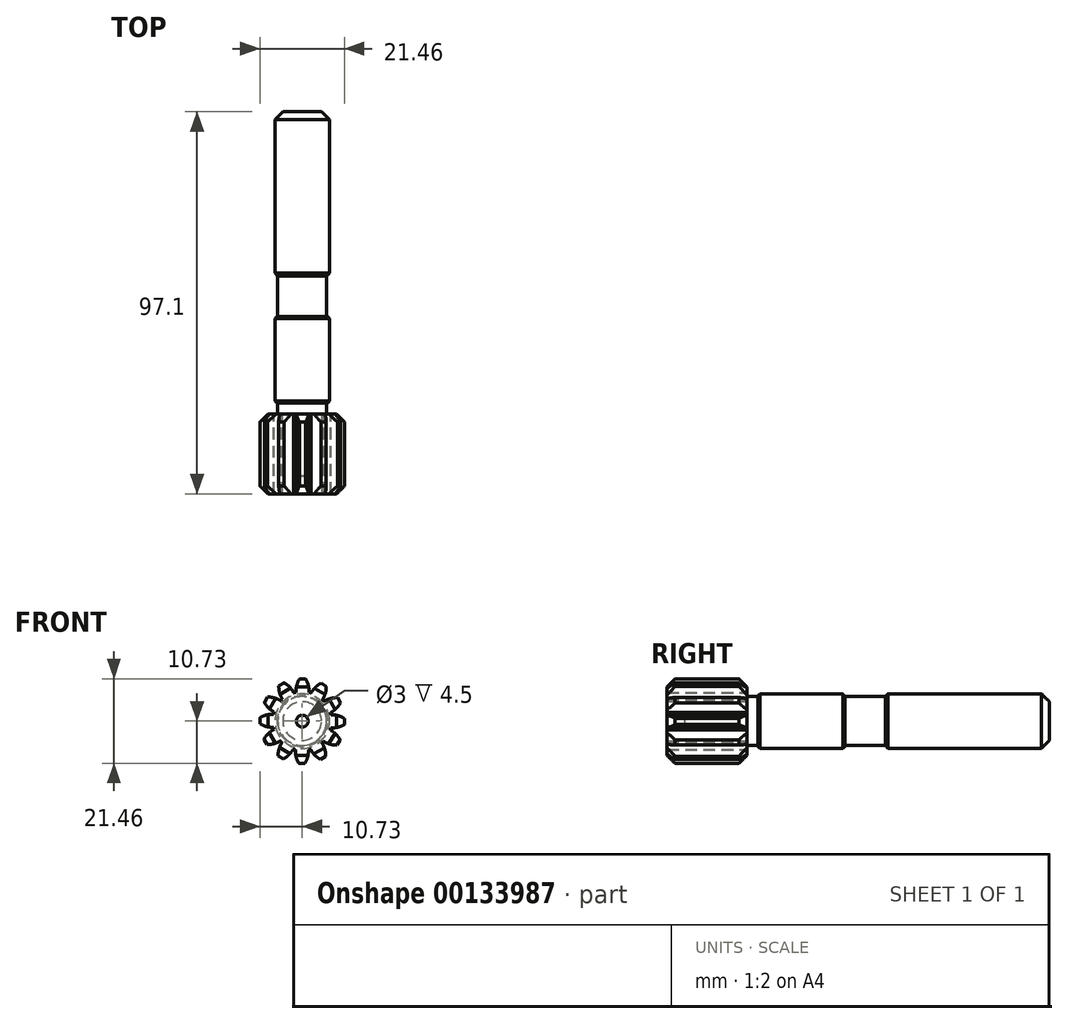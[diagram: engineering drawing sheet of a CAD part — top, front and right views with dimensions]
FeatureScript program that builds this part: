
annotation { "Feature Type Name" : "Feature", "Feature Type Description" : "" }
export const myFeature = defineFeature(function(context is Context, id is Id, definition is map)
    precondition{}
    {
        {
            var Q0;
            Q0=qCreatedBy(makeId("Front.planeOp"),FACE);
            var sketch = newSketch(context, id + "F0", { "sketchPlane" : qUnion([Q0])});
            skCircle(sketch, "E0", {"center": v(0, 0) * mm, "radius": 7.5 * mm});
            skCircle(sketch, "E1", {"center": v(0, 0) * mm, "radius": 10.75 * mm, "construction": true});
            skCircle(sketch, "E2", {"center": v(0, 0) * mm, "radius": 8.75 * mm, "construction": true});
            skArc(sketch, "E3", {"start": v(-0.67, 10.73) * mm, "mid": v(-1.38, 9.1) * mm, "end": v(-1.58, 7.33) * mm});
            skArc(sketch, "E4", {"start": v(1.73, 7.3) * mm, "mid": v(1.56, 9.07) * mm, "end": v(0.88, 10.71) * mm});
            skLineSegment(sketch, "E5", {"start": v(-0.67, 10.73) * mm, "end": v(0.88, 10.71) * mm});
            skLineSegment(sketch, "E6.1.0", {"start": v(-5.95, 8.95) * mm, "end": v(-4.6, 9.72) * mm});
            skArc(sketch, "E6.1.1", {"start": v(-2.15, 7.19) * mm, "mid": v(-3.18, 8.63) * mm, "end": v(-4.6, 9.72) * mm});
            skArc(sketch, "E6.1.2", {"start": v(-5.95, 8.95) * mm, "mid": v(-5.75, 7.19) * mm, "end": v(-5.04, 5.56) * mm});
            skLineSegment(sketch, "E6.2.0", {"start": v(-9.63, 4.78) * mm, "end": v(-8.84, 6.12) * mm});
            skArc(sketch, "E6.2.1", {"start": v(-5.45, 5.15) * mm, "mid": v(-7.07, 5.89) * mm, "end": v(-8.84, 6.12) * mm});
            skArc(sketch, "E6.2.2", {"start": v(-9.63, 4.78) * mm, "mid": v(-8.57, 3.35) * mm, "end": v(-7.14, 2.3) * mm});
            skLineSegment(sketch, "E6.3.0", {"start": v(-10.73, -0.67) * mm, "end": v(-10.71, 0.88) * mm});
            skArc(sketch, "E6.3.1", {"start": v(-7.3, 1.73) * mm, "mid": v(-9.07, 1.56) * mm, "end": v(-10.71, 0.88) * mm});
            skArc(sketch, "E6.3.2", {"start": v(-10.73, -0.67) * mm, "mid": v(-9.1, -1.38) * mm, "end": v(-7.33, -1.58) * mm});
            skLineSegment(sketch, "E6.4.0", {"start": v(-8.95, -5.95) * mm, "end": v(-9.72, -4.6) * mm});
            skArc(sketch, "E6.4.1", {"start": v(-7.19, -2.15) * mm, "mid": v(-8.63, -3.18) * mm, "end": v(-9.72, -4.6) * mm});
            skArc(sketch, "E6.4.2", {"start": v(-8.95, -5.95) * mm, "mid": v(-7.19, -5.75) * mm, "end": v(-5.56, -5.04) * mm});
            skLineSegment(sketch, "E6.5.0", {"start": v(-4.78, -9.63) * mm, "end": v(-6.12, -8.84) * mm});
            skArc(sketch, "E6.5.1", {"start": v(-5.15, -5.45) * mm, "mid": v(-5.89, -7.07) * mm, "end": v(-6.12, -8.84) * mm});
            skArc(sketch, "E6.5.2", {"start": v(-4.78, -9.63) * mm, "mid": v(-3.35, -8.57) * mm, "end": v(-2.3, -7.14) * mm});
            skLineSegment(sketch, "E6.6.0", {"start": v(0.67, -10.73) * mm, "end": v(-0.88, -10.71) * mm});
            skArc(sketch, "E6.6.1", {"start": v(-1.73, -7.3) * mm, "mid": v(-1.56, -9.07) * mm, "end": v(-0.88, -10.71) * mm});
            skArc(sketch, "E6.6.2", {"start": v(0.67, -10.73) * mm, "mid": v(1.38, -9.1) * mm, "end": v(1.58, -7.33) * mm});
            skLineSegment(sketch, "E6.7.0", {"start": v(5.95, -8.95) * mm, "end": v(4.6, -9.72) * mm});
            skArc(sketch, "E6.7.1", {"start": v(2.15, -7.19) * mm, "mid": v(3.18, -8.63) * mm, "end": v(4.6, -9.72) * mm});
            skArc(sketch, "E6.7.2", {"start": v(5.95, -8.95) * mm, "mid": v(5.75, -7.19) * mm, "end": v(5.04, -5.56) * mm});
            skLineSegment(sketch, "E6.8.0", {"start": v(9.63, -4.78) * mm, "end": v(8.84, -6.12) * mm});
            skArc(sketch, "E6.8.1", {"start": v(5.45, -5.15) * mm, "mid": v(7.07, -5.89) * mm, "end": v(8.84, -6.12) * mm});
            skArc(sketch, "E6.8.2", {"start": v(9.63, -4.78) * mm, "mid": v(8.57, -3.35) * mm, "end": v(7.14, -2.3) * mm});
            skLineSegment(sketch, "E6.9.0", {"start": v(10.73, 0.67) * mm, "end": v(10.71, -0.88) * mm});
            skArc(sketch, "E6.9.1", {"start": v(7.3, -1.73) * mm, "mid": v(9.07, -1.56) * mm, "end": v(10.71, -0.88) * mm});
            skArc(sketch, "E6.9.2", {"start": v(10.73, 0.67) * mm, "mid": v(9.1, 1.38) * mm, "end": v(7.33, 1.58) * mm});
            skLineSegment(sketch, "E6.10.0", {"start": v(8.95, 5.95) * mm, "end": v(9.72, 4.6) * mm});
            skArc(sketch, "E6.10.1", {"start": v(7.19, 2.15) * mm, "mid": v(8.63, 3.18) * mm, "end": v(9.72, 4.6) * mm});
            skArc(sketch, "E6.10.2", {"start": v(8.95, 5.95) * mm, "mid": v(7.19, 5.75) * mm, "end": v(5.56, 5.04) * mm});
            skLineSegment(sketch, "E6.11.0", {"start": v(4.78, 9.63) * mm, "end": v(6.12, 8.84) * mm});
            skArc(sketch, "E6.11.1", {"start": v(5.15, 5.45) * mm, "mid": v(5.89, 7.07) * mm, "end": v(6.12, 8.84) * mm});
            skArc(sketch, "E6.11.2", {"start": v(4.78, 9.63) * mm, "mid": v(3.35, 8.57) * mm, "end": v(2.3, 7.14) * mm});
            skSolve(sketch);
        }
        {
            var Q0;
            {var subQ0=sQuery(id+"F0.wireOp",EDGE,"E3");Q0=makeQuery(id+"F0.imprint","IMPRINT",FACE,{"disambiguationData":[TD([[makeQuery(id+"F0.imprint","IMPRINT",EDGE,{"derivedFrom":subQ0}),1.0]])]});}
            var Q1;
            {var subQ0=sQuery(id+"F0.wireOp",EDGE,"E0");var subQ15=makeQuery(id+"F0.imprint","INTERSECT",VERTEX,{"derivedFrom":[subQ0,sQuery(id+"F0.wireOp",EDGE,"E6.9.2")]});Q1=makeQuery(id+"F0.imprint","IMPRINT",FACE,{"disambiguationData":[TD([[makeQuery(id+"F0.imprint","IMPRINT",EDGE,{"disambiguationData":[TD([[subQ15,-1.0]])],"derivedFrom":subQ0}),1.0]])]});}
            var Q2;
            Q2=makeQuery(id+"F0.imprint","IMPRINT",FACE,{"disambiguationData":[TD([[makeQuery(id+"F0.imprint","IMPRINT",EDGE,{"derivedFrom":sQuery(id+"F0.wireOp",EDGE,"E6.4.0")}),-1.0]])]});
            var Q3;
            Q3=makeQuery(id+"F0.imprint","IMPRINT",FACE,{"disambiguationData":[TD([[makeQuery(id+"F0.imprint","IMPRINT",EDGE,{"derivedFrom":sQuery(id+"F0.wireOp",EDGE,"E6.3.0")}),-1.0]])]});
            var Q4;
            Q4=makeQuery(id+"F0.imprint","IMPRINT",FACE,{"disambiguationData":[TD([[makeQuery(id+"F0.imprint","IMPRINT",EDGE,{"derivedFrom":sQuery(id+"F0.wireOp",EDGE,"E6.2.0")}),-1.0]])]});
            var Q5;
            Q5=makeQuery(id+"F0.imprint","IMPRINT",FACE,{"disambiguationData":[TD([[makeQuery(id+"F0.imprint","IMPRINT",EDGE,{"derivedFrom":sQuery(id+"F0.wireOp",EDGE,"E6.1.0")}),-1.0]])]});
            var Q6;
            Q6=makeQuery(id+"F0.imprint","IMPRINT",FACE,{"disambiguationData":[TD([[makeQuery(id+"F0.imprint","IMPRINT",EDGE,{"derivedFrom":sQuery(id+"F0.wireOp",EDGE,"E6.5.0")}),-1.0]])]});
            var Q7;
            Q7=makeQuery(id+"F0.imprint","IMPRINT",FACE,{"disambiguationData":[TD([[makeQuery(id+"F0.imprint","IMPRINT",EDGE,{"derivedFrom":sQuery(id+"F0.wireOp",EDGE,"E6.6.0")}),-1.0]])]});
            var Q8;
            Q8=makeQuery(id+"F0.imprint","IMPRINT",FACE,{"disambiguationData":[TD([[makeQuery(id+"F0.imprint","IMPRINT",EDGE,{"derivedFrom":sQuery(id+"F0.wireOp",EDGE,"E6.7.0")}),-1.0]])]});
            var Q9;
            Q9=makeQuery(id+"F0.imprint","IMPRINT",FACE,{"disambiguationData":[TD([[makeQuery(id+"F0.imprint","IMPRINT",EDGE,{"derivedFrom":sQuery(id+"F0.wireOp",EDGE,"E6.8.0")}),-1.0]])]});
            var Q10;
            Q10=makeQuery(id+"F0.imprint","IMPRINT",FACE,{"disambiguationData":[TD([[makeQuery(id+"F0.imprint","IMPRINT",EDGE,{"derivedFrom":sQuery(id+"F0.wireOp",EDGE,"E6.9.0")}),-1.0]])]});
            var Q11;
            Q11=makeQuery(id+"F0.imprint","IMPRINT",FACE,{"disambiguationData":[TD([[makeQuery(id+"F0.imprint","IMPRINT",EDGE,{"derivedFrom":sQuery(id+"F0.wireOp",EDGE,"E6.10.0")}),-1.0]])]});
            var Q12;
            Q12=makeQuery(id+"F0.imprint","IMPRINT",FACE,{"disambiguationData":[TD([[makeQuery(id+"F0.imprint","IMPRINT",EDGE,{"derivedFrom":sQuery(id+"F0.wireOp",EDGE,"E6.11.0")}),-1.0]])]});
            extrude(context, id + "F1", {"entities" : qUnion([Q0, Q1, Q2, Q3, Q4, Q5, Q6, Q7, Q8, Q9, Q10, Q11, Q12]), "depth" : 20.25 * mm});
        }
        {
            var Q0;
            Q0=makeQuery(id+"F1.opExtrude","CAP_EDGE",EDGE,{"disambiguationData":[OSD([sQuery(id+"F0.wireOp",EDGE,"E6.11.0")])],"isStart":true});
            var Q1;
            Q1=makeQuery(id+"F1.opExtrude","CAP_EDGE",EDGE,{"disambiguationData":[OSD([sQuery(id+"F0.wireOp",EDGE,"E6.11.0")])],"isStart":false});
            var Q2;
            Q2=makeQuery(id+"F1.opExtrude","CAP_EDGE",EDGE,{"disambiguationData":[OSD([sQuery(id+"F0.wireOp",EDGE,"E5")])],"isStart":false});
            var Q3;
            Q3=makeQuery(id+"F1.opExtrude","CAP_EDGE",EDGE,{"disambiguationData":[OSD([sQuery(id+"F0.wireOp",EDGE,"E5")])],"isStart":true});
            var Q4;
            Q4=makeQuery(id+"F1.opExtrude","CAP_EDGE",EDGE,{"disambiguationData":[OSD([sQuery(id+"F0.wireOp",EDGE,"E6.1.0")])],"isStart":false});
            var Q5;
            Q5=makeQuery(id+"F1.opExtrude","CAP_EDGE",EDGE,{"disambiguationData":[OSD([sQuery(id+"F0.wireOp",EDGE,"E6.2.0")])],"isStart":false});
            var Q6;
            Q6=makeQuery(id+"F1.opExtrude","CAP_EDGE",EDGE,{"disambiguationData":[OSD([sQuery(id+"F0.wireOp",EDGE,"E6.3.0")])],"isStart":false});
            var Q7;
            Q7=makeQuery(id+"F1.opExtrude","CAP_EDGE",EDGE,{"disambiguationData":[OSD([sQuery(id+"F0.wireOp",EDGE,"E6.10.0")])],"isStart":false});
            var Q8;
            Q8=makeQuery(id+"F1.opExtrude","CAP_EDGE",EDGE,{"disambiguationData":[OSD([sQuery(id+"F0.wireOp",EDGE,"E6.9.0")])],"isStart":false});
            var Q9;
            Q9=makeQuery(id+"F1.opExtrude","CAP_EDGE",EDGE,{"disambiguationData":[OSD([sQuery(id+"F0.wireOp",EDGE,"E6.8.0")])],"isStart":false});
            var Q10;
            Q10=makeQuery(id+"F1.opExtrude","CAP_EDGE",EDGE,{"disambiguationData":[OSD([sQuery(id+"F0.wireOp",EDGE,"E6.7.0")])],"isStart":false});
            var Q11;
            Q11=makeQuery(id+"F1.opExtrude","CAP_EDGE",EDGE,{"disambiguationData":[OSD([sQuery(id+"F0.wireOp",EDGE,"E6.6.0")])],"isStart":false});
            var Q12;
            Q12=makeQuery(id+"F1.opExtrude","CAP_EDGE",EDGE,{"disambiguationData":[OSD([sQuery(id+"F0.wireOp",EDGE,"E6.5.0")])],"isStart":false});
            var Q13;
            Q13=makeQuery(id+"F1.opExtrude","CAP_EDGE",EDGE,{"disambiguationData":[OSD([sQuery(id+"F0.wireOp",EDGE,"E6.4.0")])],"isStart":false});
            var Q14;
            Q14=makeQuery(id+"F1.opExtrude","CAP_EDGE",EDGE,{"disambiguationData":[OSD([sQuery(id+"F0.wireOp",EDGE,"E6.10.0")])],"isStart":true});
            var Q15;
            Q15=makeQuery(id+"F1.opExtrude","CAP_EDGE",EDGE,{"disambiguationData":[OSD([sQuery(id+"F0.wireOp",EDGE,"E6.9.0")])],"isStart":true});
            var Q16;
            Q16=makeQuery(id+"F1.opExtrude","CAP_EDGE",EDGE,{"disambiguationData":[OSD([sQuery(id+"F0.wireOp",EDGE,"E6.8.0")])],"isStart":true});
            var Q17;
            Q17=makeQuery(id+"F1.opExtrude","CAP_EDGE",EDGE,{"disambiguationData":[OSD([sQuery(id+"F0.wireOp",EDGE,"E6.7.0")])],"isStart":true});
            var Q18;
            Q18=makeQuery(id+"F1.opExtrude","CAP_EDGE",EDGE,{"disambiguationData":[OSD([sQuery(id+"F0.wireOp",EDGE,"E6.6.0")])],"isStart":true});
            var Q19;
            Q19=makeQuery(id+"F1.opExtrude","CAP_EDGE",EDGE,{"disambiguationData":[OSD([sQuery(id+"F0.wireOp",EDGE,"E6.5.0")])],"isStart":true});
            var Q20;
            Q20=makeQuery(id+"F1.opExtrude","CAP_EDGE",EDGE,{"disambiguationData":[OSD([sQuery(id+"F0.wireOp",EDGE,"E6.4.0")])],"isStart":true});
            var Q21;
            Q21=makeQuery(id+"F1.opExtrude","CAP_EDGE",EDGE,{"disambiguationData":[OSD([sQuery(id+"F0.wireOp",EDGE,"E6.1.0")])],"isStart":true});
            var Q22;
            Q22=makeQuery(id+"F1.opExtrude","CAP_EDGE",EDGE,{"disambiguationData":[OSD([sQuery(id+"F0.wireOp",EDGE,"E6.2.0")])],"isStart":true});
            var Q23;
            Q23=makeQuery(id+"F1.opExtrude","CAP_EDGE",EDGE,{"disambiguationData":[OSD([sQuery(id+"F0.wireOp",EDGE,"E6.3.0")])],"isStart":true});
            chamfer(context, id + "F2", {"entities" : qUnion([Q0, Q1, Q2, Q3, Q4, Q5, Q6, Q7, Q8, Q9, Q10, Q11, Q12, Q13, Q14, Q15, Q16, Q17, Q18, Q19, Q20, Q21, Q22, Q23]), "chamferType" : ChamferType.OFFSET_ANGLE, "width" : 2 * mm, "oppositeDirection" : false, "angle" : 45 * degree, "tangentPropagation" : true});
        }
        {
            var Q0;
            Q0=makeQuery(id+"F1.opExtrude","CAP_FACE",FACE,{"disambiguationData":[OSD([sQuery(id+"F0.wireOp",EDGE,"E0"),sQuery(id+"F0.wireOp",EDGE,"E3"),sQuery(id+"F0.wireOp",EDGE,"E4"),sQuery(id+"F0.wireOp",EDGE,"E5"),sQuery(id+"F0.wireOp",EDGE,"E6.1.0"),sQuery(id+"F0.wireOp",EDGE,"E6.1.1"),sQuery(id+"F0.wireOp",EDGE,"E6.1.2"),sQuery(id+"F0.wireOp",EDGE,"E6.2.0"),sQuery(id+"F0.wireOp",EDGE,"E6.2.1"),sQuery(id+"F0.wireOp",EDGE,"E6.2.2"),sQuery(id+"F0.wireOp",EDGE,"E6.3.0"),sQuery(id+"F0.wireOp",EDGE,"E6.3.1"),sQuery(id+"F0.wireOp",EDGE,"E6.3.2"),sQuery(id+"F0.wireOp",EDGE,"E6.4.0"),sQuery(id+"F0.wireOp",EDGE,"E6.4.1"),sQuery(id+"F0.wireOp",EDGE,"E6.4.2"),sQuery(id+"F0.wireOp",EDGE,"E6.5.0"),sQuery(id+"F0.wireOp",EDGE,"E6.5.1"),sQuery(id+"F0.wireOp",EDGE,"E6.5.2"),sQuery(id+"F0.wireOp",EDGE,"E6.6.0"),sQuery(id+"F0.wireOp",EDGE,"E6.6.1"),sQuery(id+"F0.wireOp",EDGE,"E6.6.2"),sQuery(id+"F0.wireOp",EDGE,"E6.7.0"),sQuery(id+"F0.wireOp",EDGE,"E6.7.1"),sQuery(id+"F0.wireOp",EDGE,"E6.7.2"),sQuery(id+"F0.wireOp",EDGE,"E6.8.0"),sQuery(id+"F0.wireOp",EDGE,"E6.8.1"),sQuery(id+"F0.wireOp",EDGE,"E6.8.2"),sQuery(id+"F0.wireOp",EDGE,"E6.9.0"),sQuery(id+"F0.wireOp",EDGE,"E6.9.1"),sQuery(id+"F0.wireOp",EDGE,"E6.9.2"),sQuery(id+"F0.wireOp",EDGE,"E6.10.0"),sQuery(id+"F0.wireOp",EDGE,"E6.10.1"),sQuery(id+"F0.wireOp",EDGE,"E6.10.2"),sQuery(id+"F0.wireOp",EDGE,"E6.11.0"),sQuery(id+"F0.wireOp",EDGE,"E6.11.1"),sQuery(id+"F0.wireOp",EDGE,"E6.11.2")])],"isStart":false});
            var sketch = newSketch(context, id + "F3", { "sketchPlane" : qUnion([Q0])});
            skPoint(sketch, "E7", {"position": v(0, 0) * mm});
            skCircle(sketch, "E8", {"center": v(0, 0) * mm, "radius": 1.5 * mm});
            skSolve(sketch);
        }
        {
            var Q0;
            Q0=makeQuery(id+"F3.imprint","IMPRINT",FACE,{"disambiguationData":[TD([[makeQuery(id+"F3.imprint","IMPRINT",EDGE,{"derivedFrom":sQuery(id+"F3.wireOp",EDGE,"E8")}),1.0]])]});
            extrude(context, id + "F4", {"entities" : qUnion([Q0]), "operationType" : NewBodyOperationType.REMOVE, "oppositeDirection" : true, "depth" : 4.5 * mm});
        }
        {
            var Q0;
            Q0=makeQuery(id+"F1.opExtrude","CAP_FACE",FACE,{"disambiguationData":[OSD([sQuery(id+"F0.wireOp",EDGE,"E0"),sQuery(id+"F0.wireOp",EDGE,"E3"),sQuery(id+"F0.wireOp",EDGE,"E4"),sQuery(id+"F0.wireOp",EDGE,"E5"),sQuery(id+"F0.wireOp",EDGE,"E6.1.0"),sQuery(id+"F0.wireOp",EDGE,"E6.1.1"),sQuery(id+"F0.wireOp",EDGE,"E6.1.2"),sQuery(id+"F0.wireOp",EDGE,"E6.2.0"),sQuery(id+"F0.wireOp",EDGE,"E6.2.1"),sQuery(id+"F0.wireOp",EDGE,"E6.2.2"),sQuery(id+"F0.wireOp",EDGE,"E6.3.0"),sQuery(id+"F0.wireOp",EDGE,"E6.3.1"),sQuery(id+"F0.wireOp",EDGE,"E6.3.2"),sQuery(id+"F0.wireOp",EDGE,"E6.4.0"),sQuery(id+"F0.wireOp",EDGE,"E6.4.1"),sQuery(id+"F0.wireOp",EDGE,"E6.4.2"),sQuery(id+"F0.wireOp",EDGE,"E6.5.0"),sQuery(id+"F0.wireOp",EDGE,"E6.5.1"),sQuery(id+"F0.wireOp",EDGE,"E6.5.2"),sQuery(id+"F0.wireOp",EDGE,"E6.6.0"),sQuery(id+"F0.wireOp",EDGE,"E6.6.1"),sQuery(id+"F0.wireOp",EDGE,"E6.6.2"),sQuery(id+"F0.wireOp",EDGE,"E6.7.0"),sQuery(id+"F0.wireOp",EDGE,"E6.7.1"),sQuery(id+"F0.wireOp",EDGE,"E6.7.2"),sQuery(id+"F0.wireOp",EDGE,"E6.8.0"),sQuery(id+"F0.wireOp",EDGE,"E6.8.1"),sQuery(id+"F0.wireOp",EDGE,"E6.8.2"),sQuery(id+"F0.wireOp",EDGE,"E6.9.0"),sQuery(id+"F0.wireOp",EDGE,"E6.9.1"),sQuery(id+"F0.wireOp",EDGE,"E6.9.2"),sQuery(id+"F0.wireOp",EDGE,"E6.10.0"),sQuery(id+"F0.wireOp",EDGE,"E6.10.1"),sQuery(id+"F0.wireOp",EDGE,"E6.10.2"),sQuery(id+"F0.wireOp",EDGE,"E6.11.0"),sQuery(id+"F0.wireOp",EDGE,"E6.11.1"),sQuery(id+"F0.wireOp",EDGE,"E6.11.2")])],"isStart":true});
            var sketch = newSketch(context, id + "F5", { "sketchPlane" : qUnion([Q0])});
            skCircle(sketch, "E9", {"center": v(0, 0) * mm, "radius": 6.22 * mm});
            skSolve(sketch);
        }
        {
            var Q0;
            Q0=qSketchRegion(id+"F5",true);
            extrude(context, id + "F6", {"entities" : qUnion([Q0]), "operationType" : NewBodyOperationType.ADD, "depth" : 2.85 * mm});
        }
        {
            var Q0;
            Q0=makeQuery(id+"F6.opExtrude","CAP_FACE",FACE,{"disambiguationData":[OSD([sQuery(id+"F5.wireOp",EDGE,"E9")])],"isStart":false});
            var sketch = newSketch(context, id + "F7", { "sketchPlane" : qUnion([Q0])});
            skCircle(sketch, "E10", {"center": v(0, 0) * mm, "radius": 6.93 * mm});
            skSolve(sketch);
        }
        {
            var Q0;
            Q0=qSketchRegion(id+"F7",true);
            extrude(context, id + "F8", {"entities" : qUnion([Q0]), "operationType" : NewBodyOperationType.ADD, "depth" : 22 * mm});
        }
        {
            var Q0;
            Q0=makeQuery(id+"F8.opExtrude","CAP_FACE",FACE,{"disambiguationData":[OSD([sQuery(id+"F7.wireOp",EDGE,"E10")])],"isStart":false});
            var sketch = newSketch(context, id + "F9", { "sketchPlane" : qUnion([Q0])});
            skCircle(sketch, "E11", {"center": v(0, 0) * mm, "radius": 6.23 * mm});
            skSolve(sketch);
        }
        {
            var Q0;
            Q0=qSketchRegion(id+"F9",true);
            extrude(context, id + "F10", {"entities" : qUnion([Q0]), "operationType" : NewBodyOperationType.ADD, "depth" : 9 * mm});
        }
        {
            var Q0;
            Q0=makeQuery(id+"F8.opExtrude","SWEPT_FACE",FACE,{"disambiguationData":[OSD([sQuery(id+"F7.wireOp",EDGE,"E10")])]});
            chamfer(context, id + "F11", {"entities" : qUnion([Q0]), "chamferType" : ChamferType.OFFSET_ANGLE, "width" : .5 * mm, "oppositeDirection" : false, "angle" : 45 * degree, "tangentPropagation" : true});
        }
        {
            var Q0;
            Q0=makeQuery(id+"F10.opExtrude","CAP_FACE",FACE,{"disambiguationData":[OSD([sQuery(id+"F9.wireOp",EDGE,"E11")])],"isStart":false});
            var sketch = newSketch(context, id + "F12", { "sketchPlane" : qUnion([Q0])});
            skCircle(sketch, "E12", {"center": v(0, 0) * mm, "radius": 6.92 * mm});
            skSolve(sketch);
        }
        {
            var Q0;
            Q0=qSketchRegion(id+"F12",true);
            extrude(context, id + "F13", {"entities" : qUnion([Q0]), "operationType" : NewBodyOperationType.ADD, "depth" : 43 * mm});
        }
        {
            var Q0;
            Q0=makeQuery(id+"F13.opExtrude","SWEPT_FACE",FACE,{"disambiguationData":[OSD([sQuery(id+"F12.wireOp",EDGE,"E12")])]});
            chamfer(context, id + "F14", {"entities" : qUnion([Q0]), "chamferType" : ChamferType.OFFSET_ANGLE, "width" : 2 * mm, "oppositeDirection" : false, "angle" : 45 * degree, "tangentPropagation" : true});
        }
    });
